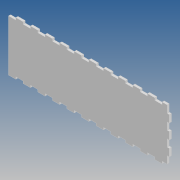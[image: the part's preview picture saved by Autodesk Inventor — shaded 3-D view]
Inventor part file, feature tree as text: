
AUTODESK INVENTOR PART (.ipt)
format: ipt  version: 2020 (Build 240168000, 168)  size: 193,024 bytes
history: native  units: mm
features: extrude x4, sketch x4, pattern_linear x3, other x1
ambient origin geometry x8: Origin, YZ Plane, XZ Plane, XY Plane, X Axis, Y Axis, Z Axis, Center Point
bodies: Body1 (feature_tree)
feature tree (12):
  other  "Твердое тело1"
  extrude  "Выдавливание1"  Depth=10.0mm
  pattern_linear  "Прямоуг.массив1"  Spacing1=3.0mm  [1 undecoded]
  extrude  "Выдавливание2"  Depth=3.0mm TaperAngle=0.0deg
  extrude  "Выдавливание3"  Depth=110.0mm
  pattern_linear  "Прямоуг.массив2"  Count1=7  [1 undecoded]
  extrude  "Выдавливание4"  Depth=3.0mm TaperAngle=0.0deg
  pattern_linear  "Прямоуг.массив3"  Spacing1=10.0mm  [1 undecoded]
  sketch  "Эскиз1"
  sketch  "Эскиз2"
  sketch  "Эскиз3"
  sketch  "Эскиз4"
note: 3 required parameter values undecoded (feature->parameter linkage not recoverable at this tier; creation-order binding heuristic only, values carry confidence <= 0.55)
